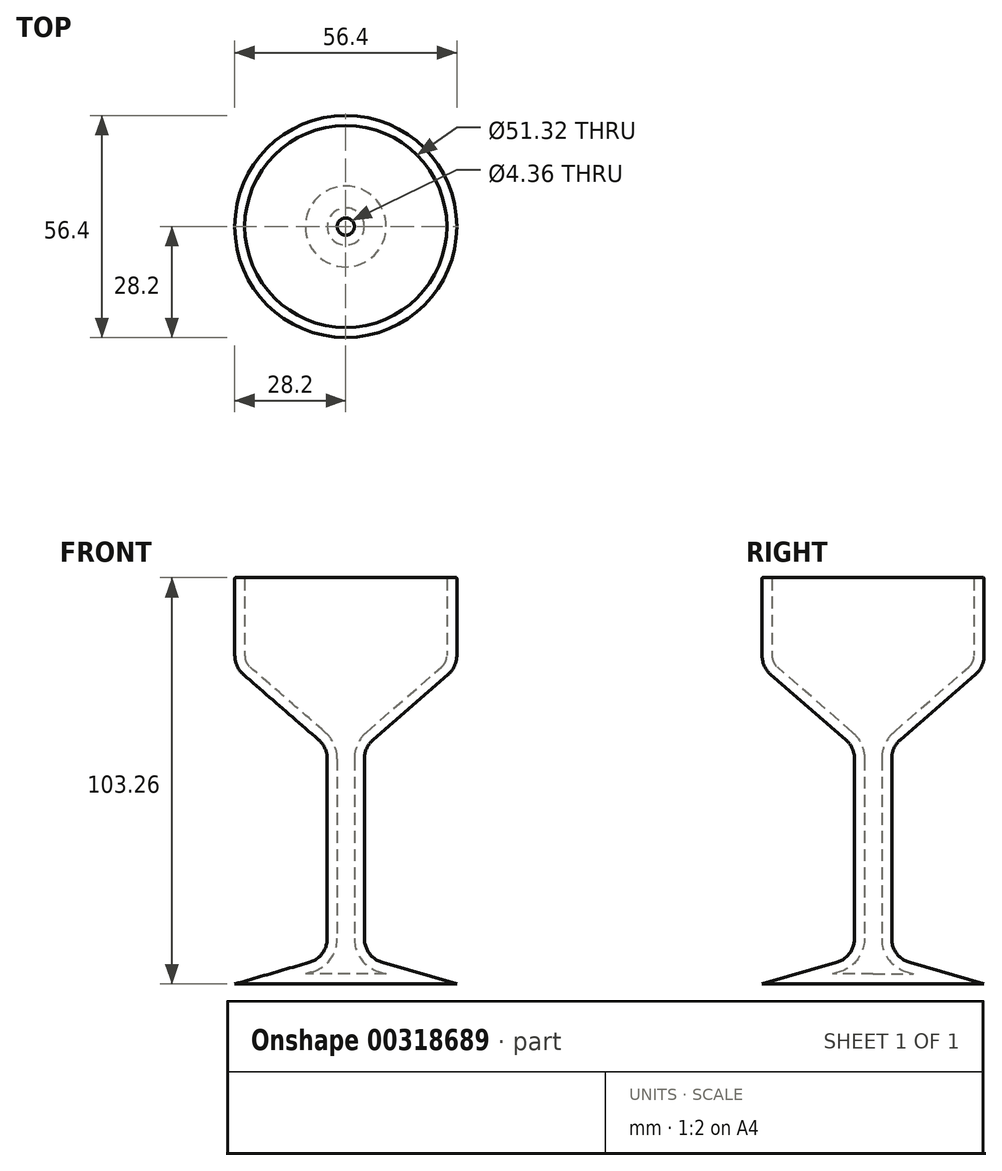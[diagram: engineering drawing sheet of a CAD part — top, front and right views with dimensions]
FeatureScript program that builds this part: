
annotation { "Feature Type Name" : "Feature", "Feature Type Description" : "" }
export const myFeature = defineFeature(function(context is Context, id is Id, definition is map)
    precondition{}
    {
        {
            var Q0;
            Q0=qCreatedBy(makeId("Front.planeOp"),FACE);
            var sketch = newSketch(context, id + "F0", { "sketchPlane" : qUnion([Q0])});
            skLineSegment(sketch, "E0", {"start": v(0, 47.34) * mm, "end": v(-28.2, 47.34) * mm});
            skLineSegment(sketch, "E1", {"start": v(-28.2, 47.34) * mm, "end": v(-28.2, 27.52) * mm});
            skLineSegment(sketch, "E2", {"start": v(-26.02, 22.73) * mm, "end": v(-6.9, 6.1) * mm});
            skLineSegment(sketch, "E3", {"start": v(-4.72, 1.32) * mm, "end": v(-4.72, -44.35) * mm});
            skLineSegment(sketch, "E4", {"start": v(-9.3, -50.46) * mm, "end": v(-25.9, -55.25) * mm});
            skLineSegment(sketch, "E5", {"start": v(-25.9, -55.25) * mm, "end": v(-28.2, -55.92) * mm});
            skLineSegment(sketch, "E6", {"start": v(-28.2, -55.92) * mm, "end": v(0, -55.92) * mm});
            skLineSegment(sketch, "E7", {"start": v(0, -55.92) * mm, "end": v(0, 47.34) * mm});
            skPoint(sketch, "E8.visualSharp", {"position": v(-4.72, -49.13) * mm});
            skArc(sketch, "E8.filletArc", {"start": v(-9.3, -50.46) * mm, "mid": v(-6, -48.17) * mm, "end": v(-4.72, -44.35) * mm});
            skPoint(sketch, "E9.visualSharp", {"position": v(-4.72, 4.21) * mm});
            skArc(sketch, "E9.filletArc", {"start": v(-4.72, 1.32) * mm, "mid": v(-5.3, 3.95) * mm, "end": v(-6.9, 6.1) * mm});
            skPoint(sketch, "E10.visualSharp", {"position": v(-28.2, 24.63) * mm});
            skArc(sketch, "E10.filletArc", {"start": v(-28.2, 27.52) * mm, "mid": v(-27.63, 24.89) * mm, "end": v(-26.02, 22.73) * mm});
            skSolve(sketch);
        }
        {
            var Q0;
            Q0=makeQuery(id+"F0.imprint","IMPRINT",FACE,{"disambiguationData":[TD([[makeQuery(id+"F0.imprint","IMPRINT",EDGE,{"derivedFrom":sQuery(id+"F0.wireOp",EDGE,"E0")}),1.0]])]});
            var Q1;
            Q1=sQuery(id+"F0.wireOp",EDGE,"E7");
            revolve(context, id + "F1", {"entities" : qUnion([Q0]), "axis" : qUnion([Q1]), "revolveType" : RevolveType.SYMMETRIC, "angle" : 360 * degree});
        }
        {
            var Q0;
            Q0=makeQuery(id+"F1.opRevolve","SWEPT_FACE",FACE,{"disambiguationData":[OSD([sQuery(id+"F0.wireOp",EDGE,"E0")])]});
            shell(context, id + "F2", {"entities" : qUnion([Q0]), "thickness" : 2.54 * mm});
        }
        {
            var Q0;
            Q0=makeQuery(id+"F1.opRevolve","SWEPT_EDGE",EDGE,{"disambiguationData":[OSD([sQuery(id+"F0.wireOp",EDGE,"E0"),sQuery(id+"F0.wireOp",EDGE,"E1")])]});
            var Q1;
            Q1=makeQuery(id+"F2.opShell","OFFSET_EDGE",EDGE,{"disambiguationData":[OSD([sQuery(id+"F0.wireOp",EDGE,"E2"),sQuery(id+"F0.wireOp",EDGE,"E10.filletArc")])]});
            var Q2;
            Q2=makeQuery(id+"F2.opShell","OFFSET_EDGE",EDGE,{"disambiguationData":[OSD([sQuery(id+"F0.wireOp",EDGE,"E0"),sQuery(id+"F0.wireOp",EDGE,"E1")])]});
            var Q3;
            Q3=makeQuery(id+"F2.opShell","OFFSET_EDGE",EDGE,{"disambiguationData":[OSD([sQuery(id+"F0.wireOp",EDGE,"E1"),sQuery(id+"F0.wireOp",EDGE,"E10.filletArc")])]});
            var Q4;
            Q4=makeQuery(id+"F1.opRevolve","SWEPT_FACE",FACE,{"disambiguationData":[OSD([sQuery(id+"F0.wireOp",EDGE,"E1")])]});
            fillet(context, id + "F3", {"entities" : qUnion([Q0, Q1, Q2, Q3, Q4]), "radius" : 0.25 * mm, "tangentPropagation" : true, "allowEdgeOverflow" : false});
        }
    });
